# Revit family: Tub_Filler-DXV-Randall-D3510295X_Series
name_source: partatom
category: Plumbing Fixtures
revit_build: Autodesk Revit 2014 (Build: 20130308_1515(x64)
units: mm (PartAtom-declared; Revit-internal decimal feet)

## types (8) — shared parameters
Assembly Code = D2010710
CW Connection = Yes
CWFU = 3
Cold Water Connection Diameter = 1/2"
Cold Water Connection Radius = 1/4"
Cold Water Connection Width = 3"
Default Elevation = 0"
Description = Transitional Floor Mount Tub Filler with Randall® Handles
Flow Rate = 2.0 gpm (7.6 L/min)
HW Connection = Yes
HWFU = 3
Height = 28 7/8"
Hot Water Connection Diameter = 1"
Hot Water Connection Radius = 1/4"
Hot Water Connection Width = 3"
Installation Type = Deck Mounted
Length = 11 3/4"
Manufacturer = DXV
Price = Prices may vary. Please consult Manufacturer Representative for most up-to-date price list.
Product Documentation Link = https://dxv01.blob.core.windows.net
Product Page URL = https://www.dxv.com
URL = http://www.dxv.com
Vent Connection = No
WFU = 4
Warranty Documentation Link = https://www.dxv.com
Waste Connection = No
Width = 12 5/8"

## per-type parameters (varying)
| type | ADA Compliant | Cross Handles | Finish | Lever Handles | Material |
| D35102954.144 | No | Yes | Metal-DXV-144-Brushed Nickel | No | Metal-DXV-144-Brushed Nickel |
| D35102950.100 | Yes | No | Metal-DXV-100-Polished Chrome | Yes | Metal-DXV-100-Polished Chrome |
| D35102954.150 | No | Yes | Metal-DXV-150-Platinum Nickel | No | Metal-DXV-150-Platinum Nickel |
| D35102950.144 | Yes | No | Metal-DXV-144-Brushed Nickel | Yes | Metal-DXV-144-Brushed Nickel |
| D35102950.150 | Yes | No | Metal-DXV-150-Platinum Nickel | Yes | Metal-DXV-150-Platinum Nickel |
| D35102950.427 | Yes | No | Metal-DXV-427-Satin Brass | Yes | Metal-DXV-427-Satin Brass |
| D35102954.100 | No | Yes | Metal-DXV-100-Polished Chrome | No | Metal-DXV-100-Polished Chrome |
| D35102954.427 | No | Yes | Metal-DXV-427-Satin Brass | No | Metal-DXV-427-Satin Brass |

note: column(s) folded — value = type name in every type: Model

## geometry (parser evidence)
native form markers: Sweep x1
no freeform markers — native parametric forms only
